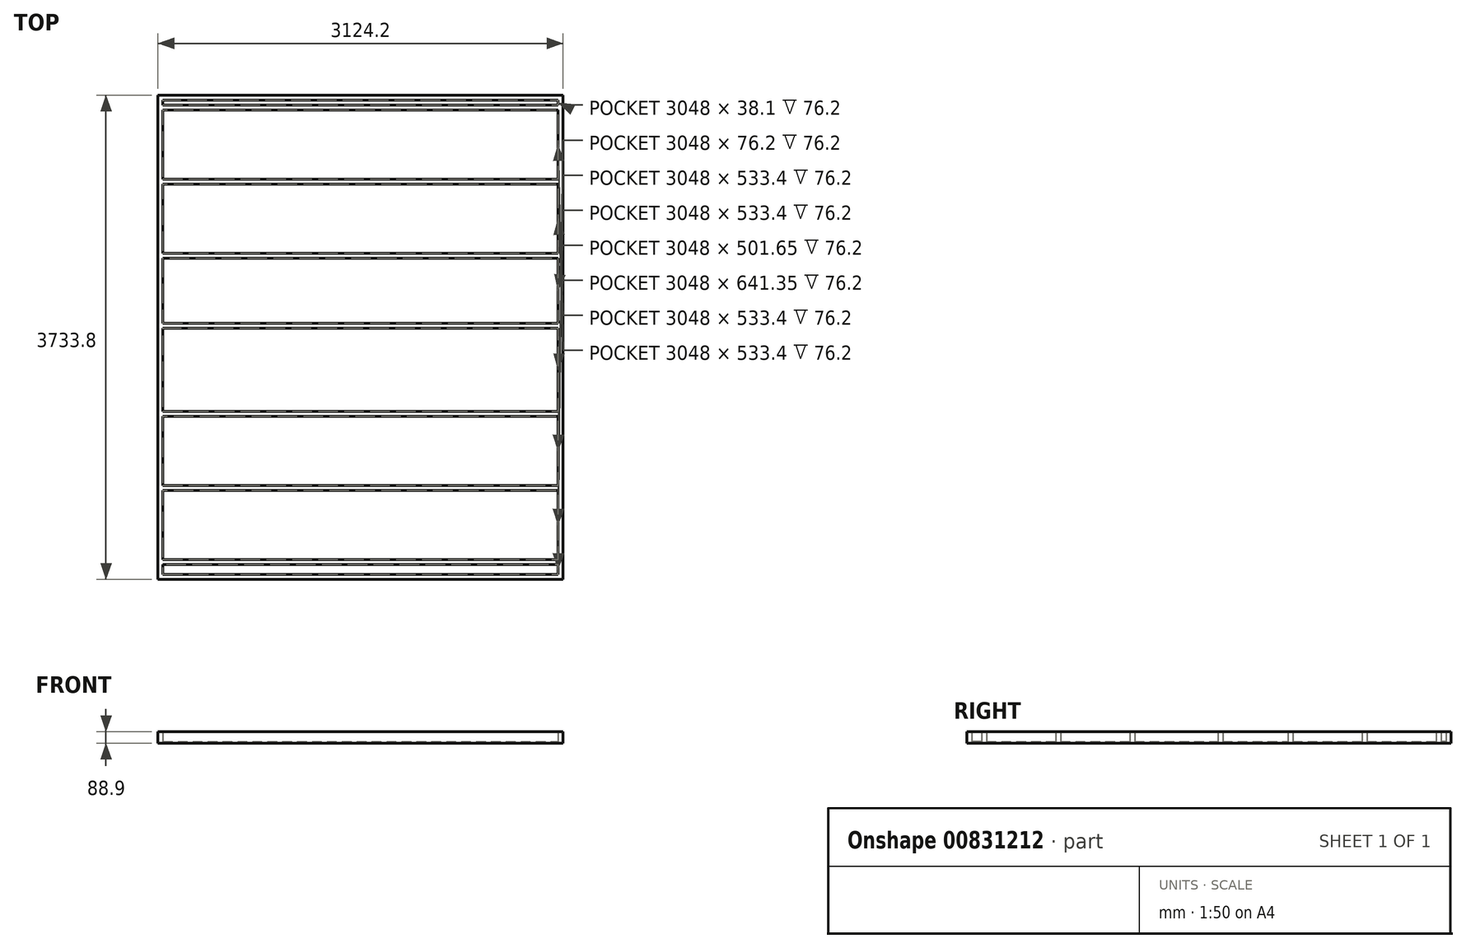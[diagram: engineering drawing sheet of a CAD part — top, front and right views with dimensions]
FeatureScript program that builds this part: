
annotation { "Feature Type Name" : "Feature", "Feature Type Description" : "" }
export const myFeature = defineFeature(function(context is Context, id is Id, definition is map)
    precondition{}
    {
        {
            var Q0;
            Q0=qCreatedBy(makeId("Top.planeOp"),FACE);
            var sketch = newSketch(context, id + "F0", { "sketchPlane" : qUnion([Q0])});
            skLineSegment(sketch, "E0.bottom", {"start": v(1562.1, 1866.9) * mm, "end": v(-1562.1, 1866.9) * mm});
            skLineSegment(sketch, "E0.top", {"start": v(1562.1, -1866.9) * mm, "end": v(-1562.1, -1866.9) * mm});
            skLineSegment(sketch, "E0.left", {"start": v(1562.1, 1866.9) * mm, "end": v(1562.1, -1866.9) * mm});
            skLineSegment(sketch, "E0.right", {"start": v(-1562.1, 1866.9) * mm, "end": v(-1562.1, -1866.9) * mm});
            skPoint(sketch, "E0.middle", {"position": v(0, 0) * mm});
            skSolve(sketch);
        }
        {
            var Q0;
            Q0 = qSketchRegion(id + "F0", true);
            extrude(context, id + "F1", {"entities" : qUnion([Q0]), "depth" : 12.7 * mm, "offsetDistance" : 25.4 * mm});
        }
        {
            var Q0;
            Q0=makeQuery(id+"F1.opExtrude","CAP_FACE",FACE,{"disambiguationData":[OSD([sQuery(id+"F0.wireOp",EDGE,"E0.bottom"),sQuery(id+"F0.wireOp",EDGE,"E0.top"),sQuery(id+"F0.wireOp",EDGE,"E0.left"),sQuery(id+"F0.wireOp",EDGE,"E0.right")])],"isStart":false});
            var sketch = newSketch(context, id + "F2", { "sketchPlane" : qUnion([Q0])});
            skLineSegment(sketch, "E1.bottom", {"start": v(-1562.1, 1866.9) * mm, "end": v(1562.1, 1866.9) * mm});
            skLineSegment(sketch, "E1.top", {"start": v(-1562.1, 1828.8) * mm, "end": v(1562.1, 1828.8) * mm});
            skLineSegment(sketch, "E1.left", {"start": v(-1562.1, 1866.9) * mm, "end": v(-1562.1, 1828.8) * mm});
            skLineSegment(sketch, "E1.right", {"start": v(1562.1, 1866.9) * mm, "end": v(1562.1, 1828.8) * mm});
            skLineSegment(sketch, "E2.bottom", {"start": v(1562.1, 1828.8) * mm, "end": v(1524, 1828.8) * mm});
            skLineSegment(sketch, "E2.top", {"start": v(1562.1, -1828.8) * mm, "end": v(1524, -1828.8) * mm});
            skLineSegment(sketch, "E2.left", {"start": v(1562.1, 1828.8) * mm, "end": v(1562.1, -1828.8) * mm});
            skLineSegment(sketch, "E2.right", {"start": v(1524, 1828.8) * mm, "end": v(1524, -38.1) * mm});
            skLineSegment(sketch, "E3.bottom", {"start": v(1562.1, -1828.8) * mm, "end": v(-1562.1, -1828.8) * mm});
            skLineSegment(sketch, "E3.top", {"start": v(1562.1, -1866.9) * mm, "end": v(-1562.1, -1866.9) * mm});
            skLineSegment(sketch, "E3.left", {"start": v(1562.1, -1828.8) * mm, "end": v(1562.1, -1866.9) * mm});
            skLineSegment(sketch, "E3.right", {"start": v(-1562.1, -1828.8) * mm, "end": v(-1562.1, -1866.9) * mm});
            skLineSegment(sketch, "E4.bottom", {"start": v(-1562.1, -1828.8) * mm, "end": v(-1524, -1828.8) * mm});
            skLineSegment(sketch, "E4.top", {"start": v(-1562.1, 1828.8) * mm, "end": v(-1524, 1828.8) * mm});
            skLineSegment(sketch, "E4.left", {"start": v(-1562.1, -1828.8) * mm, "end": v(-1562.1, 1828.8) * mm});
            skLineSegment(sketch, "E5.bottom", {"start": v(-1524, 1219.2) * mm, "end": v(1524, 1219.2) * mm});
            skLineSegment(sketch, "E5.top", {"start": v(-1524, 1181.1) * mm, "end": v(1524, 1181.1) * mm});
            skLineSegment(sketch, "E5.left", {"start": v(-1524, 1219.2) * mm, "end": v(-1524, 1181.1) * mm});
            skLineSegment(sketch, "E5.right", {"start": v(1524, 1219.2) * mm, "end": v(1524, 1181.1) * mm});
            skLineSegment(sketch, "E6.bottom", {"start": v(-1524, 647.7) * mm, "end": v(1524, 647.7) * mm});
            skLineSegment(sketch, "E6.top", {"start": v(-1524, 609.6) * mm, "end": v(1524, 609.6) * mm});
            skLineSegment(sketch, "E6.left", {"start": v(-1524, 647.7) * mm, "end": v(-1524, 609.6) * mm});
            skLineSegment(sketch, "E6.right", {"start": v(1524, 647.7) * mm, "end": v(1524, 609.6) * mm});
            skLineSegment(sketch, "E7.bottom", {"start": v(-1524, -571.5) * mm, "end": v(1524, -571.5) * mm});
            skLineSegment(sketch, "E7.top", {"start": v(-1524, -609.6) * mm, "end": v(1524, -609.6) * mm});
            skLineSegment(sketch, "E7.left", {"start": v(-1524, -571.5) * mm, "end": v(-1524, -609.6) * mm});
            skLineSegment(sketch, "E7.right", {"start": v(1524, -571.5) * mm, "end": v(1524, -609.6) * mm});
            skLineSegment(sketch, "E8.bottom", {"start": v(-1524, -1143) * mm, "end": v(1524, -1143) * mm});
            skLineSegment(sketch, "E8.top", {"start": v(-1524, -1181.1) * mm, "end": v(1524, -1181.1) * mm});
            skLineSegment(sketch, "E8.left", {"start": v(-1524, -1143) * mm, "end": v(-1524, -1181.1) * mm});
            skLineSegment(sketch, "E8.right", {"start": v(1524, -1143) * mm, "end": v(1524, -1181.1) * mm});
            skLineSegment(sketch, "E9.bottom", {"start": v(1524, -1714.5) * mm, "end": v(-1524, -1714.5) * mm});
            skLineSegment(sketch, "E9.top", {"start": v(1524, -1752.6) * mm, "end": v(-1524, -1752.6) * mm});
            skLineSegment(sketch, "E9.left", {"start": v(1524, -1714.5) * mm, "end": v(1524, -1752.6) * mm});
            skLineSegment(sketch, "E9.right", {"start": v(-1524, -1714.5) * mm, "end": v(-1524, -1752.6) * mm});
            skLineSegment(sketch, "E10.bottom", {"start": v(-1524, 1790.7) * mm, "end": v(1524, 1790.7) * mm});
            skLineSegment(sketch, "E10.top", {"start": v(-1524, 1752.6) * mm, "end": v(1524, 1752.6) * mm});
            skLineSegment(sketch, "E10.left", {"start": v(-1524, 1790.7) * mm, "end": v(-1524, 1752.6) * mm});
            skLineSegment(sketch, "E10.right", {"start": v(1524, 1790.7) * mm, "end": v(1524, 1752.6) * mm});
            skLineSegment(sketch, "E11", {"start": v(-1524, -1828.8) * mm, "end": v(-1524, 1828.8) * mm});
            skLineSegment(sketch, "E12.trimOffspring", {"start": v(1524, -38.1) * mm, "end": v(1524, -1828.8) * mm});
            skLineSegment(sketch, "E13.bottom", {"start": v(-1524, 107.95) * mm, "end": v(1524, 107.95) * mm});
            skLineSegment(sketch, "E13.top", {"start": v(-1524, 69.85) * mm, "end": v(1524, 69.85) * mm});
            skLineSegment(sketch, "E13.left", {"start": v(-1524, 107.95) * mm, "end": v(-1524, 69.85) * mm});
            skLineSegment(sketch, "E13.right", {"start": v(1524, 107.95) * mm, "end": v(1524, 69.85) * mm});
            skSolve(sketch);
        }
        {
            var Q0;
            Q0 = qSketchRegion(id + "F2", true);
            var Q1;
            {var subQ0=sQuery(id+"F2.wireOp",EDGE,"E10.bottom");Q1=makeQuery(id+"F2.imprint","IMPRINT",FACE,{"disambiguationData":[TD([[makeQuery(id+"F2.imprint","IMPRINT",EDGE,{"derivedFrom":subQ0}),-1.0]])]});}
            var Q2;
            {var subQ0=sQuery(id+"F2.wireOp",EDGE,"E5.bottom");Q2=makeQuery(id+"F2.imprint","IMPRINT",FACE,{"disambiguationData":[TD([[makeQuery(id+"F2.imprint","IMPRINT",EDGE,{"derivedFrom":subQ0}),-1.0]])]});}
            var Q3;
            {var subQ0=sQuery(id+"F2.wireOp",EDGE,"E6.bottom");Q3=makeQuery(id+"F2.imprint","IMPRINT",FACE,{"disambiguationData":[TD([[makeQuery(id+"F2.imprint","IMPRINT",EDGE,{"derivedFrom":subQ0}),-1.0]])]});}
            var Q4;
            Q4=makeQuery(id+"F2.imprint","IMPRINT",FACE,{"disambiguationData":[TD([[makeQuery(id+"F2.imprint","IMPRINT",EDGE,{"derivedFrom":sQuery(id+"F2.wireOp",EDGE,"E13.bottom")}),-1.0]])]});
            var Q5;
            {var subQ0=sQuery(id+"F2.wireOp",EDGE,"E7.bottom");Q5=makeQuery(id+"F2.imprint","IMPRINT",FACE,{"disambiguationData":[TD([[makeQuery(id+"F2.imprint","IMPRINT",EDGE,{"derivedFrom":subQ0}),-1.0]])]});}
            var Q6;
            {var subQ0=sQuery(id+"F2.wireOp",EDGE,"E9.bottom");Q6=makeQuery(id+"F2.imprint","IMPRINT",FACE,{"disambiguationData":[TD([[makeQuery(id+"F2.imprint","IMPRINT",EDGE,{"derivedFrom":subQ0}),1.0]])]});}
            var Q7;
            {var subQ0=sQuery(id+"F2.wireOp",EDGE,"E8.bottom");Q7=makeQuery(id+"F2.imprint","IMPRINT",FACE,{"disambiguationData":[TD([[makeQuery(id+"F2.imprint","IMPRINT",EDGE,{"derivedFrom":subQ0}),-1.0]])]});}
            extrude(context, id + "F3", {"entities" : qUnion([Q0, Q1, Q2, Q3, Q4, Q5, Q6, Q7]), "operationType" : NewBodyOperationType.ADD, "depth" : 76.2 * mm, "offsetDistance" : 25.4 * mm});
        }
    });
